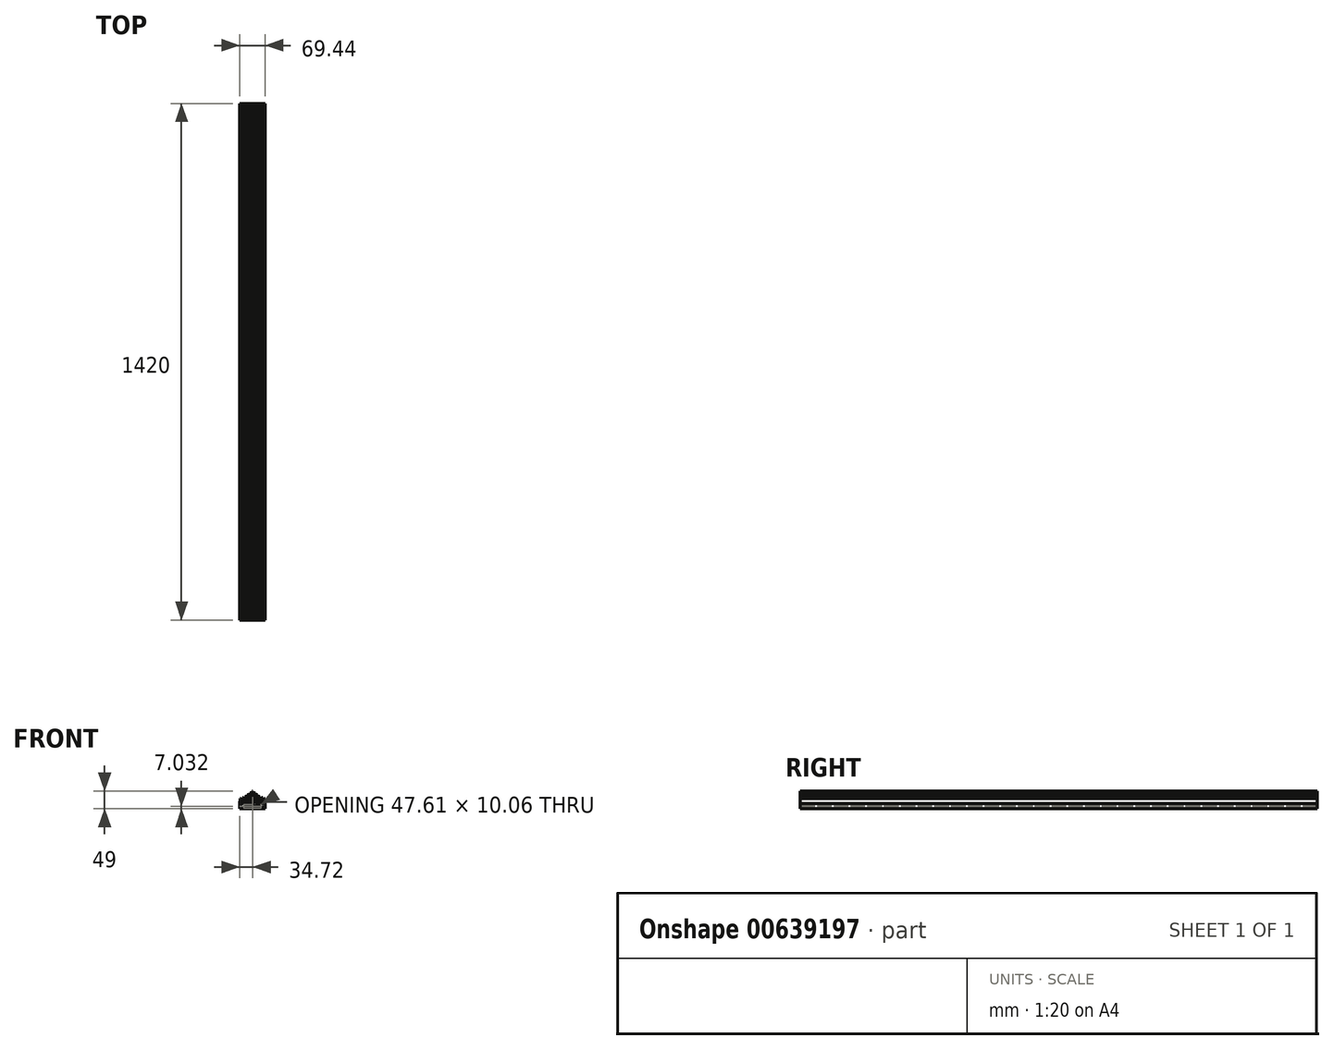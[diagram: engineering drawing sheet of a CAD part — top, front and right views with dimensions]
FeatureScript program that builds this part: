
annotation { "Feature Type Name" : "Feature", "Feature Type Description" : "" }
export const myFeature = defineFeature(function(context is Context, id is Id, definition is map)
    precondition{}
    {
        {
            var Q0;
            Q0=qCreatedBy(makeId("Front.planeOp"),FACE);
            var sketch = newSketch(context, id + "F0", { "sketchPlane" : qUnion([Q0])});
            skPoint(sketch, "E0.visualSharp", {"position": v(0, -3.5) * mm});
            skPoint(sketch, "E1.visualSharp", {"position": v(-32.72, 3.5) * mm});
            skLineSegment(sketch, "E2", {"start": v(-32.97, 18.5) * mm, "end": v(-34.47, 18.5) * mm});
            skLineSegment(sketch, "E3", {"start": v(-34.47, 18.5) * mm, "end": v(-34.72, 3.5) * mm});
            skLineSegment(sketch, "E4", {"start": v(-32.97, 18.5) * mm, "end": v(-32.72, 3.5) * mm});
            skLineSegment(sketch, "E5", {"start": v(-32.72, 3.5) * mm, "end": v(-28, 3.5) * mm});
            skLineSegment(sketch, "E6.1.0.0", {"start": v(-26.25, 21) * mm, "end": v(-26, 3.5) * mm});
            skLineSegment(sketch, "E6.1.0.2", {"start": v(-26, 3.5) * mm, "end": v(-21.24, 3.5) * mm});
            skPoint(sketch, "E6.1.0.3", {"position": v(-26, 3.5) * mm});
            skLineSegment(sketch, "E6.1.0.4", {"start": v(-26.25, 21) * mm, "end": v(-27.75, 21) * mm});
            skLineSegment(sketch, "E6.3.0.0", {"start": v(-12.87, 28.5) * mm, "end": v(-12.62, 3.5) * mm});
            skLineSegment(sketch, "E6.3.0.2", {"start": v(-12.62, 3.5) * mm, "end": v(-7.75, 3.5) * mm});
            skPoint(sketch, "E6.3.0.3", {"position": v(-12.62, 3.5) * mm});
            skLineSegment(sketch, "E6.3.0.4", {"start": v(-12.87, 28.5) * mm, "end": v(-14.37, 28.5) * mm});
            skLineSegment(sketch, "E6.4.0.0", {"start": v(-6, 33.5) * mm, "end": v(-5.75, 3.5) * mm});
            skLineSegment(sketch, "E6.4.0.2", {"start": v(-5.75, 3.5) * mm, "end": v(-1, 3.5) * mm});
            skPoint(sketch, "E6.4.0.3", {"position": v(-5.75, 3.5) * mm});
            skLineSegment(sketch, "E6.4.0.4", {"start": v(-6, 33.5) * mm, "end": v(-7.5, 33.5) * mm});
            skLineSegment(sketch, "E7", {"start": v(-27.75, 21) * mm, "end": v(-28, 3.5) * mm});
            skLineSegment(sketch, "E8", {"start": v(-20.99, 23.5) * mm, "end": v(-21.24, 3.5) * mm});
            skLineSegment(sketch, "E9", {"start": v(-0.75, 38.5) * mm, "end": v(-1, 3.5) * mm});
            skLineSegment(sketch, "E10", {"start": v(-7.75, 3.5) * mm, "end": v(-7.5, 33.5) * mm});
            skLineSegment(sketch, "E11", {"start": v(-14.37, 28.5) * mm, "end": v(-14.62, 3.5) * mm});
            skPoint(sketch, "E12", {"position": v(-34.72, 3.5) * mm});
            skLineSegment(sketch, "E13", {"start": v(0, -3.5) * mm, "end": v(-7.75, -3.5) * mm});
            skLineSegment(sketch, "E14", {"start": v(-34.72, 3.5) * mm, "end": v(-34.72, -10.5) * mm});
            skLineSegment(sketch, "E15", {"start": v(-7.75, -3.5) * mm, "end": v(-10.32, -0.44) * mm});
            skLineSegment(sketch, "E16", {"start": v(-11.21, -3.5) * mm, "end": v(-12.82, -1.58) * mm});
            skLineSegment(sketch, "E17", {"start": v(-28.55, -8) * mm, "end": v(-28.55, -6.5) * mm});
            skLineSegment(sketch, "E18", {"start": v(-28.55, -6.5) * mm, "end": v(-27.55, -6.5) * mm});
            skLineSegment(sketch, "E19", {"start": v(-25.3, -3.5) * mm, "end": v(-25.3, -8.5) * mm});
            skLineSegment(sketch, "E20", {"start": v(-23.8, -8.5) * mm, "end": v(-23.8, -3.5) * mm});
            skLineSegment(sketch, "E21.trimOffspring", {"start": v(-23.8, -3.5) * mm, "end": v(-11.21, -3.5) * mm});
            skLineSegment(sketch, "E22", {"start": v(-25.3, -3.5) * mm, "end": v(-27.72, -3.5) * mm});
            skLineSegment(sketch, "E23", {"start": v(-34.72, -10.5) * mm, "end": v(-27.55, -10.5) * mm});
            skLineSegment(sketch, "E24", {"start": v(-27.55, -6.5) * mm, "end": v(-27.55, -10.5) * mm});
            skLineSegment(sketch, "E25", {"start": v(-32.05, -6) * mm, "end": v(-32.05, -8) * mm});
            skLineSegment(sketch, "E26", {"start": v(-32.05, -8) * mm, "end": v(-28.55, -8) * mm});
            skLineSegment(sketch, "E27", {"start": v(-32.05, -6) * mm, "end": v(-27.72, -3.5) * mm});
            skLineSegment(sketch, "E28", {"start": v(-10.32, -0.44) * mm, "end": v(-10.32, 0.31) * mm});
            skLineSegment(sketch, "E29", {"start": v(-12.82, -1.58) * mm, "end": v(-12.82, 0.31) * mm});
            skArc(sketch, "E30", {"start": v(-10.32, 0.31) * mm, "mid": v(-11.57, 1.56) * mm, "end": v(-12.82, 0.31) * mm});
            skPoint(sketch, "E31", {"position": v(-19.24, 3.5) * mm});
            skLineSegment(sketch, "E32", {"start": v(-20.99, 23.5) * mm, "end": v(-19.49, 23.5) * mm});
            skLineSegment(sketch, "E33", {"start": v(-19.49, 23.5) * mm, "end": v(-19.24, 3.5) * mm});
            skLineSegment(sketch, "E34", {"start": v(-19.24, 3.5) * mm, "end": v(-14.62, 3.5) * mm});
            skPoint(sketch, "E35", {"position": v(-33.72, 3.5) * mm});
            skPoint(sketch, "E36", {"position": v(-27, 3.5) * mm});
            skPoint(sketch, "E37", {"position": v(-20.24, 3.5) * mm});
            skPoint(sketch, "E38", {"position": v(-13.62, 3.5) * mm});
            skPoint(sketch, "E39", {"position": v(-6.75, 3.5) * mm});
            skLineSegment(sketch, "E40", {"start": v(-0.75, 38.5) * mm, "end": v(0, 38.5) * mm});
            skLineSegment(sketch, "E41", {"start": v(0, -3.5) * mm, "end": v(0, 38.5) * mm});
            skLineSegment(sketch, "E42", {"start": v(-27.1, -3.5) * mm, "end": v(-25.3, -3.5) * mm});
            skLineSegment(sketch, "E43", {"start": v(-25.3, -8.5) * mm, "end": v(-23.8, -8.5) * mm});
            skSolve(sketch);
        }
        {
            var Q0;
            Q0=qSketchRegion(id+"F0",true);
            extrude(context, id + "F1", {"entities" : qUnion([Q0]), "depth" : 1420 * mm, "offsetDistance" : 25 * mm});
        }
        {
            var Q0;
            {var subQ0=makeQuery(id+"F1.opExtrude","CAP_FACE",FACE,{"disambiguationData":[OSD([sQuery(id+"F0.wireOp",EDGE,"E2"),sQuery(id+"F0.wireOp",EDGE,"E3"),sQuery(id+"F0.wireOp",EDGE,"E4"),sQuery(id+"F0.wireOp",EDGE,"E5"),sQuery(id+"F0.wireOp",EDGE,"E6.1.0.0"),sQuery(id+"F0.wireOp",EDGE,"E6.1.0.2"),sQuery(id+"F0.wireOp",EDGE,"E6.1.0.4"),sQuery(id+"F0.wireOp",EDGE,"E6.3.0.0"),sQuery(id+"F0.wireOp",EDGE,"E6.3.0.2"),sQuery(id+"F0.wireOp",EDGE,"E6.3.0.4"),sQuery(id+"F0.wireOp",EDGE,"E6.4.0.0"),sQuery(id+"F0.wireOp",EDGE,"E6.4.0.2"),sQuery(id+"F0.wireOp",EDGE,"E6.4.0.4"),sQuery(id+"F0.wireOp",EDGE,"E7"),sQuery(id+"F0.wireOp",EDGE,"E8"),sQuery(id+"F0.wireOp",EDGE,"E9"),sQuery(id+"F0.wireOp",EDGE,"E10"),sQuery(id+"F0.wireOp",EDGE,"E11"),sQuery(id+"F0.wireOp",EDGE,"E13"),sQuery(id+"F0.wireOp",EDGE,"E14"),sQuery(id+"F0.wireOp",EDGE,"E15"),sQuery(id+"F0.wireOp",EDGE,"E16"),sQuery(id+"F0.wireOp",EDGE,"E17"),sQuery(id+"F0.wireOp",EDGE,"E18"),sQuery(id+"F0.wireOp",EDGE,"E19"),sQuery(id+"F0.wireOp",EDGE,"E20"),sQuery(id+"F0.wireOp",EDGE,"E21.trimOffspring"),sQuery(id+"F0.wireOp",EDGE,"E22"),sQuery(id+"F0.wireOp",EDGE,"E23"),sQuery(id+"F0.wireOp",EDGE,"E24"),sQuery(id+"F0.wireOp",EDGE,"E25"),sQuery(id+"F0.wireOp",EDGE,"E26"),sQuery(id+"F0.wireOp",EDGE,"E27"),sQuery(id+"F0.wireOp",EDGE,"E28"),sQuery(id+"F0.wireOp",EDGE,"E29"),sQuery(id+"F0.wireOp",EDGE,"E30"),sQuery(id+"F0.wireOp",EDGE,"E32"),sQuery(id+"F0.wireOp",EDGE,"E33"),sQuery(id+"F0.wireOp",EDGE,"E34"),sQuery(id+"F0.wireOp",EDGE,"E40"),sQuery(id+"F0.wireOp",EDGE,"E41"),sQuery(id+"F0.wireOp",EDGE,"E42"),sQuery(id+"F0.wireOp",EDGE,"E43")])],"isStart":false});Q0=makeQuery(id+"F4.boolean.opBoolean","MERGE",FACE,{"derivedFrom":[subQ0,makeQuery(id+"F4.opPattern","COPY",FACE,{"derivedFrom":subQ0,"instanceName":"1"})]});}
            var sketch = newSketch(context, id + "F2", { "sketchPlane" : qUnion([Q0])});
            skLineSegment(sketch, "E44", {"start": v(-25.3, -3.5) * mm, "end": v(-25.3, -8.5) * mm});
            skLineSegment(sketch, "E45", {"start": v(-25.3, -8.5) * mm, "end": v(0, -8.5) * mm});
            skLineSegment(sketch, "E46", {"start": v(0, -8.5) * mm, "end": v(0, -10.5) * mm});
            skLineSegment(sketch, "E47", {"start": v(0, -10.5) * mm, "end": v(-27.3, -10.5) * mm});
            skLineSegment(sketch, "E48", {"start": v(-27.3, -10.5) * mm, "end": v(-27.3, -3.5) * mm});
            skLineSegment(sketch, "E49", {"start": v(-27.3, -3.5) * mm, "end": v(-25.3, -3.5) * mm});
            skSolve(sketch);
        }
        {
            var Q0;
            Q0 = qSketchRegion(id + "F2", true);
            extrude(context, id + "F3", {"entities" : qUnion([Q0]), "oppositeDirection" : true, "depth" : 1420 * mm, "offsetDistance" : 25 * mm});
        }
        {
            var Q0;
            Q0=makeQuery(id+"F1.opExtrude","SWEPT_BODY",BODY,{"disambiguationData":[OSD([sQuery(id+"F0.wireOp",EDGE,"E2"),sQuery(id+"F0.wireOp",EDGE,"E3"),sQuery(id+"F0.wireOp",EDGE,"E4"),sQuery(id+"F0.wireOp",EDGE,"E5"),sQuery(id+"F0.wireOp",EDGE,"E6.1.0.0"),sQuery(id+"F0.wireOp",EDGE,"E6.1.0.2"),sQuery(id+"F0.wireOp",EDGE,"E6.1.0.4"),sQuery(id+"F0.wireOp",EDGE,"E6.3.0.0"),sQuery(id+"F0.wireOp",EDGE,"E6.3.0.2"),sQuery(id+"F0.wireOp",EDGE,"E6.3.0.4"),sQuery(id+"F0.wireOp",EDGE,"E6.4.0.0"),sQuery(id+"F0.wireOp",EDGE,"E6.4.0.2"),sQuery(id+"F0.wireOp",EDGE,"E6.4.0.4"),sQuery(id+"F0.wireOp",EDGE,"E7"),sQuery(id+"F0.wireOp",EDGE,"E8"),sQuery(id+"F0.wireOp",EDGE,"E9"),sQuery(id+"F0.wireOp",EDGE,"E10"),sQuery(id+"F0.wireOp",EDGE,"E11"),sQuery(id+"F0.wireOp",EDGE,"E13"),sQuery(id+"F0.wireOp",EDGE,"E14"),sQuery(id+"F0.wireOp",EDGE,"E15"),sQuery(id+"F0.wireOp",EDGE,"E16"),sQuery(id+"F0.wireOp",EDGE,"E17"),sQuery(id+"F0.wireOp",EDGE,"E18"),sQuery(id+"F0.wireOp",EDGE,"E19"),sQuery(id+"F0.wireOp",EDGE,"LJRGZIwq-aAv5-vMYT-1Wya-NWjgFLSVPvfh"),sQuery(id+"F0.wireOp",EDGE,"E20"),sQuery(id+"F0.wireOp",EDGE,"E21.trimOffspring"),sQuery(id+"F0.wireOp",EDGE,"E22"),sQuery(id+"F0.wireOp",EDGE,"E23"),sQuery(id+"F0.wireOp",EDGE,"E24"),sQuery(id+"F0.wireOp",EDGE,"E25"),sQuery(id+"F0.wireOp",EDGE,"E26"),sQuery(id+"F0.wireOp",EDGE,"E27"),sQuery(id+"F0.wireOp",EDGE,"E28"),sQuery(id+"F0.wireOp",EDGE,"E29"),sQuery(id+"F0.wireOp",EDGE,"E30"),sQuery(id+"F0.wireOp",EDGE,"E32"),sQuery(id+"F0.wireOp",EDGE,"E33"),sQuery(id+"F0.wireOp",EDGE,"E34"),sQuery(id+"F0.wireOp",EDGE,"E40"),sQuery(id+"F0.wireOp",EDGE,"E41")])]});
            var Q1;
            Q1=makeQuery(id+"F1.opExtrude","SWEPT_BODY",BODY,{"disambiguationData":[OSD([sQuery(id+"F0.wireOp",EDGE,"9R7NK8zM-tC3Y-ZixV-HQ1Y-UdCP3e18fYu1"),sQuery(id+"F0.wireOp",EDGE,"hQkL2SHW-n77w-gf69-hCro-iTtwEbU04zFK"),sQuery(id+"F0.wireOp",EDGE,"g9Ot94Kp-ymDL-BriN-G1aE-UjGC9mEJR13i"),sQuery(id+"F0.wireOp",EDGE,"c3ti7Jjn-FzDr-I3oW-gQrF-BovdJvhkW4j7"),sQuery(id+"F0.wireOp",EDGE,"YMYXA4ls-wpxf-aHBe-Aeno-18cLMt04RpPS"),sQuery(id+"F0.wireOp",EDGE,"KmtUdOI4-E3le-O6Zy-3GTd-ahnRvYm0T2aJ")])]});
            var Q2;
            Q2=makeQuery(id+"F1.opExtrude","SWEPT_FACE",FACE,{"disambiguationData":[OSD([sQuery(id+"F0.wireOp",EDGE,"E41")])]});
            mirror(context, id + "F4", {"operationType" : NewBodyOperationType.ADD, "entities" : qUnion([Q0, Q1]), "mirrorPlane" : qUnion([Q2])});
        }
        {
            var Q0;
            Q0=makeQuery(id+"F3.opExtrude","SWEPT_BODY",BODY,{"disambiguationData":[OSD([sQuery(id+"F2.wireOp",EDGE,"E44"),sQuery(id+"F2.wireOp",EDGE,"E45"),sQuery(id+"F2.wireOp",EDGE,"E46"),sQuery(id+"F2.wireOp",EDGE,"E47"),sQuery(id+"F2.wireOp",EDGE,"E48"),sQuery(id+"F2.wireOp",EDGE,"E49")])]});
            var Q1;
            Q1=makeQuery(id+"F3.opExtrude","SWEPT_FACE",FACE,{"disambiguationData":[OSD([sQuery(id+"F2.wireOp",EDGE,"E46")])]});
            mirror(context, id + "F5", {"operationType" : NewBodyOperationType.ADD, "entities" : qUnion([Q0]), "mirrorPlane" : qUnion([Q1])});
        }
    });
